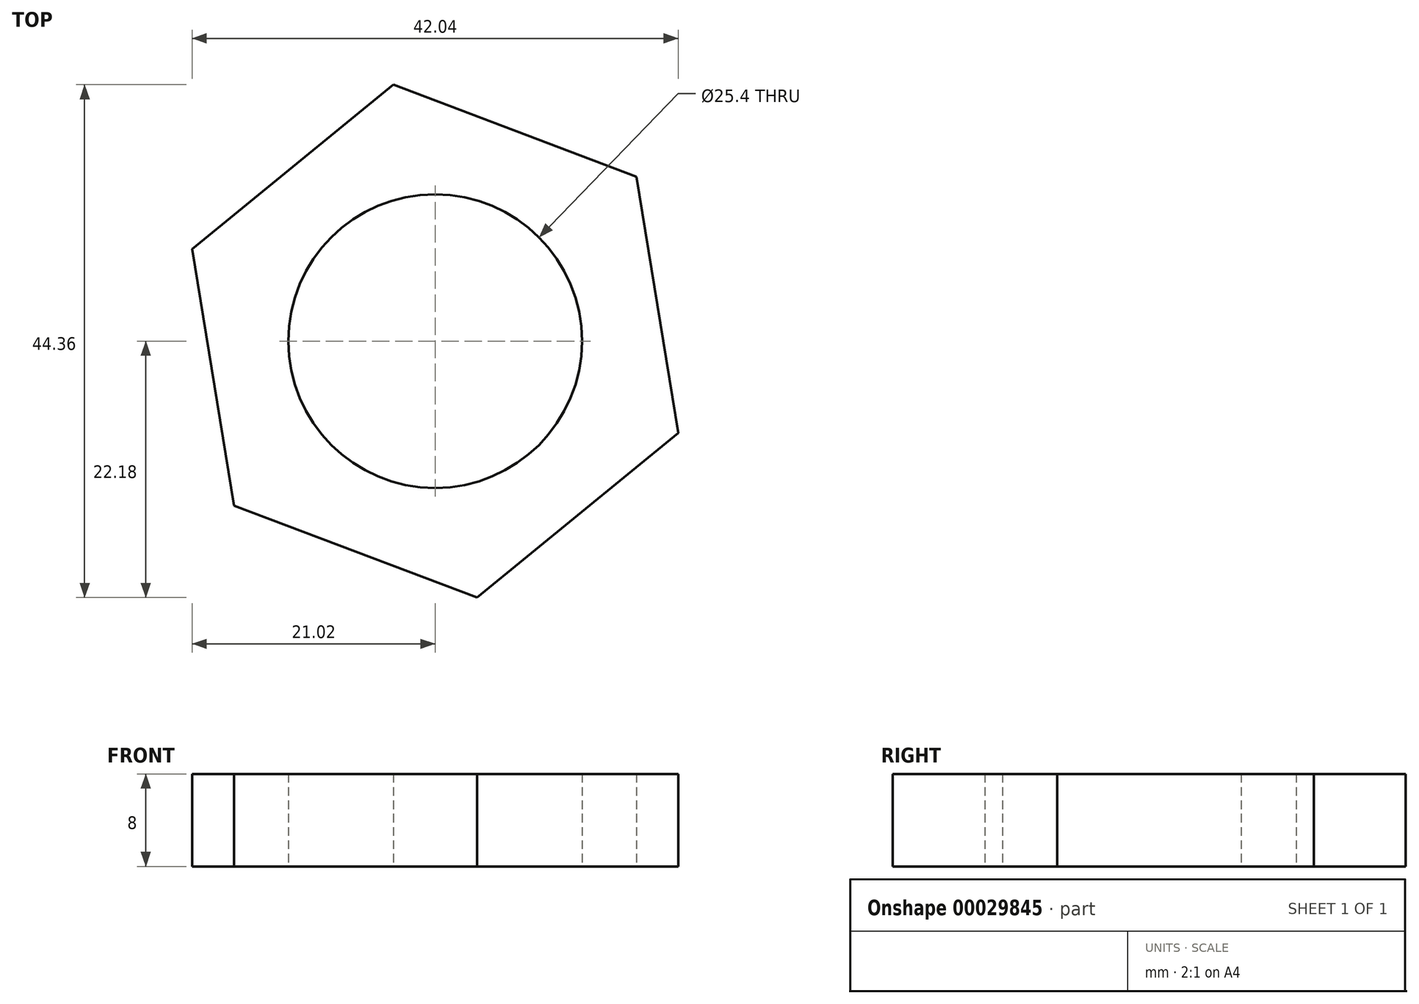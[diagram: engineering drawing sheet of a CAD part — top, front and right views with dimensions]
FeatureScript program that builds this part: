
annotation { "Feature Type Name" : "Feature", "Feature Type Description" : "" }
export const myFeature = defineFeature(function(context is Context, id is Id, definition is map)
    precondition{}
    {
        {
            var Q0;
            Q0=qCreatedBy(makeId("Top.planeOp"),FACE);
            var sketch = newSketch(context, id + "F0", { "sketchPlane" : qUnion([Q0])});
            skPoint(sketch, "E0.visualSharp", {"position": v(55.99, 31.38) * mm});
            skPoint(sketch, "E1.visualSharp", {"position": v(5.9, -10.62) * mm});
            skCircle(sketch, "E2", {"center": v(0, 0) * mm, "radius": 12.7 * mm});
            skCircle(sketch, "E3.cCircle", {"center": v(0, 0) * mm, "radius": 19.46 * mm, "construction": true});
            skLineSegment(sketch, "E3.0", {"start": v(-21.02, 7.95) * mm, "end": v(-3.62, 22.18) * mm});
            skLineSegment(sketch, "E3.1", {"start": v(-3.62, 22.18) * mm, "end": v(17.4, 14.23) * mm});
            skLineSegment(sketch, "E3.2", {"start": v(17.4, 14.23) * mm, "end": v(21.02, -7.95) * mm});
            skLineSegment(sketch, "E3.3", {"start": v(21.02, -7.95) * mm, "end": v(3.62, -22.18) * mm});
            skLineSegment(sketch, "E3.4", {"start": v(3.62, -22.18) * mm, "end": v(-17.4, -14.23) * mm});
            skLineSegment(sketch, "E3.5", {"start": v(-17.4, -14.23) * mm, "end": v(-21.02, 7.95) * mm});
            skPoint(sketch, "E3.0.midPoint", {"position": v(-12.32, 15.06) * mm});
            skSolve(sketch);
        }
        {
            var Q0;
            Q0=makeQuery(id+"F0.imprint","IMPRINT",FACE,{"disambiguationData":[TD([[makeQuery(id+"F0.imprint","IMPRINT",EDGE,{"derivedFrom":sQuery(id+"F0.wireOp",EDGE,"E2")}),-1.0]])]});
            extrude(context, id + "F1", {"entities" : qUnion([Q0]), "depth" : 8 * mm});
        }
    });
